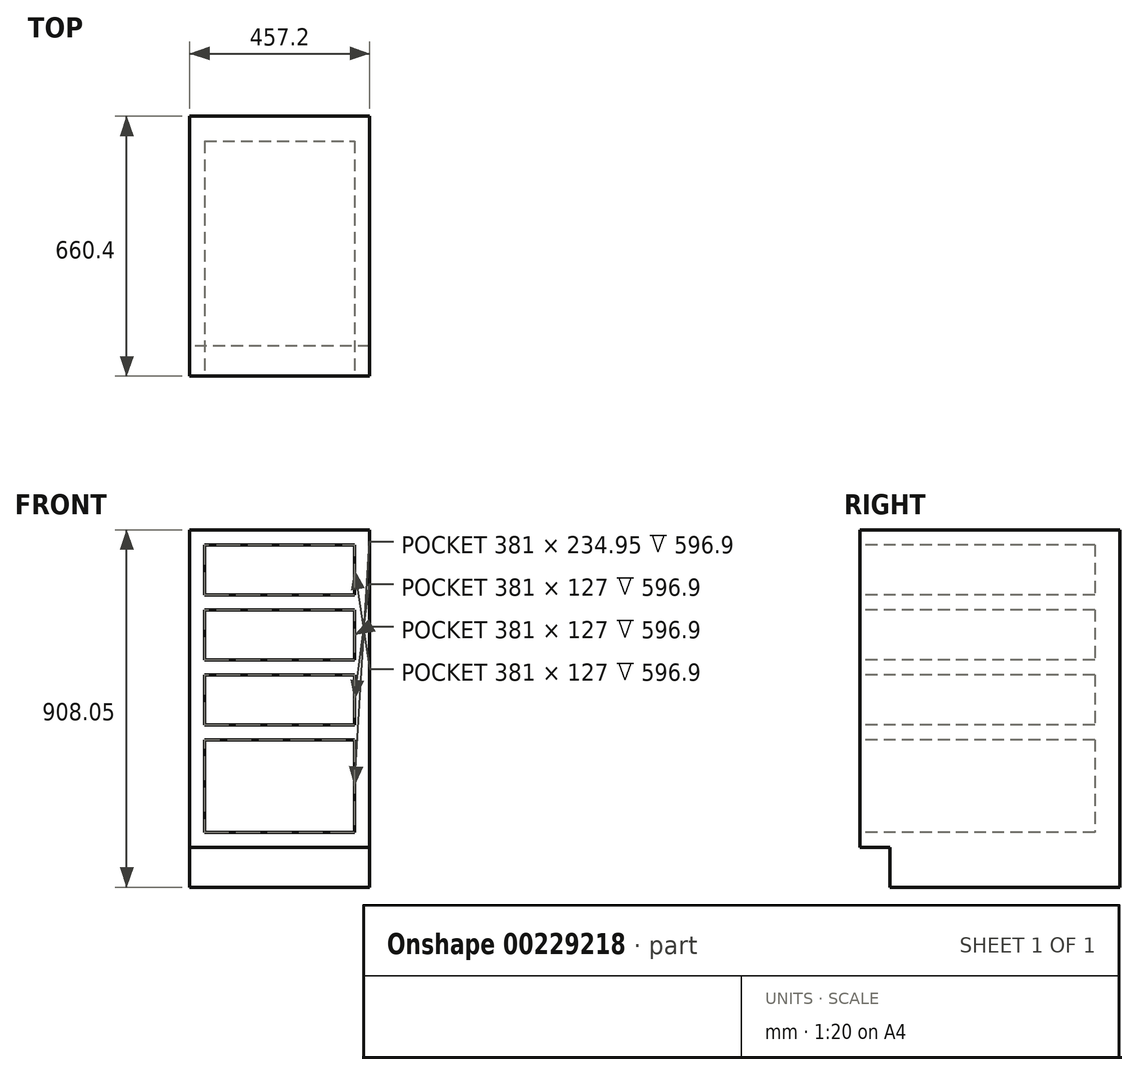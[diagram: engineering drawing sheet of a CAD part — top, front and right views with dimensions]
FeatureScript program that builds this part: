
annotation { "Feature Type Name" : "Feature", "Feature Type Description" : "" }
export const myFeature = defineFeature(function(context is Context, id is Id, definition is map)
    precondition{}
    {
        {
            var Q0;
            Q0=qCreatedBy(makeId("Right.planeOp"),FACE);
            var sketch = newSketch(context, id + "F0", { "sketchPlane" : qUnion([Q0])});
            skLineSegment(sketch, "E0", {"start": v(0, 0) * mm, "end": v(-584.2, 0) * mm});
            skLineSegment(sketch, "E1", {"start": v(-584.2, 0) * mm, "end": v(-584.2, 101.6) * mm});
            skLineSegment(sketch, "E2", {"start": v(-584.2, 101.6) * mm, "end": v(-660.4, 101.6) * mm});
            skLineSegment(sketch, "E3", {"start": v(-660.4, 101.6) * mm, "end": v(-660.4, 908.05) * mm});
            skLineSegment(sketch, "E4", {"start": v(-660.4, 908.05) * mm, "end": v(0, 908.05) * mm});
            skLineSegment(sketch, "E5", {"start": v(0, 908.05) * mm, "end": v(0, 0) * mm});
            skSolve(sketch);
        }
        {
            var Q0;
            Q0=makeQuery(id+"F0.imprint","IMPRINT",FACE,{"disambiguationData":[TD([[makeQuery(id+"F0.imprint","IMPRINT",EDGE,{"derivedFrom":sQuery(id+"F0.wireOp",EDGE,"E0")}),-1.0]])]});
            extrude(context, id + "F1", {"entities" : qUnion([Q0]), "depth" : 457.2 * mm});
        }
        {
            var Q0;
            Q0=makeQuery(id+"F1.opExtrude","SWEPT_FACE",FACE,{"disambiguationData":[OSD([sQuery(id+"F0.wireOp",EDGE,"E3")])]});
            var sketch = newSketch(context, id + "F2", { "sketchPlane" : qUnion([Q0])});
            skLineSegment(sketch, "E6.bottom", {"start": v(38.1, 869.95) * mm, "end": v(419.1, 869.95) * mm});
            skLineSegment(sketch, "E6.top", {"start": v(38.1, 742.95) * mm, "end": v(419.1, 742.95) * mm});
            skLineSegment(sketch, "E6.left", {"start": v(38.1, 869.95) * mm, "end": v(38.1, 742.95) * mm});
            skLineSegment(sketch, "E6.right", {"start": v(419.1, 869.95) * mm, "end": v(419.1, 742.95) * mm});
            skLineSegment(sketch, "E7.bottom", {"start": v(38.1, 704.85) * mm, "end": v(419.1, 704.85) * mm});
            skLineSegment(sketch, "E7.top", {"start": v(38.1, 577.85) * mm, "end": v(419.1, 577.85) * mm});
            skLineSegment(sketch, "E7.left", {"start": v(38.1, 704.85) * mm, "end": v(38.1, 577.85) * mm});
            skLineSegment(sketch, "E7.right", {"start": v(419.1, 704.85) * mm, "end": v(419.1, 577.85) * mm});
            skLineSegment(sketch, "E8.bottom", {"start": v(38.1, 539.75) * mm, "end": v(419.1, 539.75) * mm});
            skLineSegment(sketch, "E8.top", {"start": v(38.1, 412.75) * mm, "end": v(419.1, 412.75) * mm});
            skLineSegment(sketch, "E8.left", {"start": v(38.1, 539.75) * mm, "end": v(38.1, 412.75) * mm});
            skLineSegment(sketch, "E8.right", {"start": v(419.1, 539.75) * mm, "end": v(419.1, 412.75) * mm});
            skLineSegment(sketch, "E9.bottom", {"start": v(38.1, 374.65) * mm, "end": v(419.1, 374.65) * mm});
            skLineSegment(sketch, "E9.top", {"start": v(38.1, 139.7) * mm, "end": v(419.1, 139.7) * mm});
            skLineSegment(sketch, "E9.left", {"start": v(38.1, 374.65) * mm, "end": v(38.1, 139.7) * mm});
            skLineSegment(sketch, "E9.right", {"start": v(419.1, 374.65) * mm, "end": v(419.1, 139.7) * mm});
            skSolve(sketch);
        }
        {
            var Q0;
            Q0=makeQuery(id+"F2.imprint","IMPRINT",FACE,{"disambiguationData":[TD([[makeQuery(id+"F2.imprint","IMPRINT",EDGE,{"derivedFrom":sQuery(id+"F2.wireOp",EDGE,"E6.bottom")}),-1.0]])]});
            var Q1;
            Q1=makeQuery(id+"F2.imprint","IMPRINT",FACE,{"disambiguationData":[TD([[makeQuery(id+"F2.imprint","IMPRINT",EDGE,{"derivedFrom":sQuery(id+"F2.wireOp",EDGE,"E7.bottom")}),-1.0]])]});
            var Q2;
            Q2=makeQuery(id+"F2.imprint","IMPRINT",FACE,{"disambiguationData":[TD([[makeQuery(id+"F2.imprint","IMPRINT",EDGE,{"derivedFrom":sQuery(id+"F2.wireOp",EDGE,"E8.bottom")}),-1.0]])]});
            var Q3;
            Q3=makeQuery(id+"F2.imprint","IMPRINT",FACE,{"disambiguationData":[TD([[makeQuery(id+"F2.imprint","IMPRINT",EDGE,{"derivedFrom":sQuery(id+"F2.wireOp",EDGE,"E9.bottom")}),-1.0]])]});
            extrude(context, id + "F3", {"entities" : qUnion([Q0, Q1, Q2, Q3]), "operationType" : NewBodyOperationType.REMOVE, "oppositeDirection" : true, "depth" : 596.9 * mm});
        }
    });
